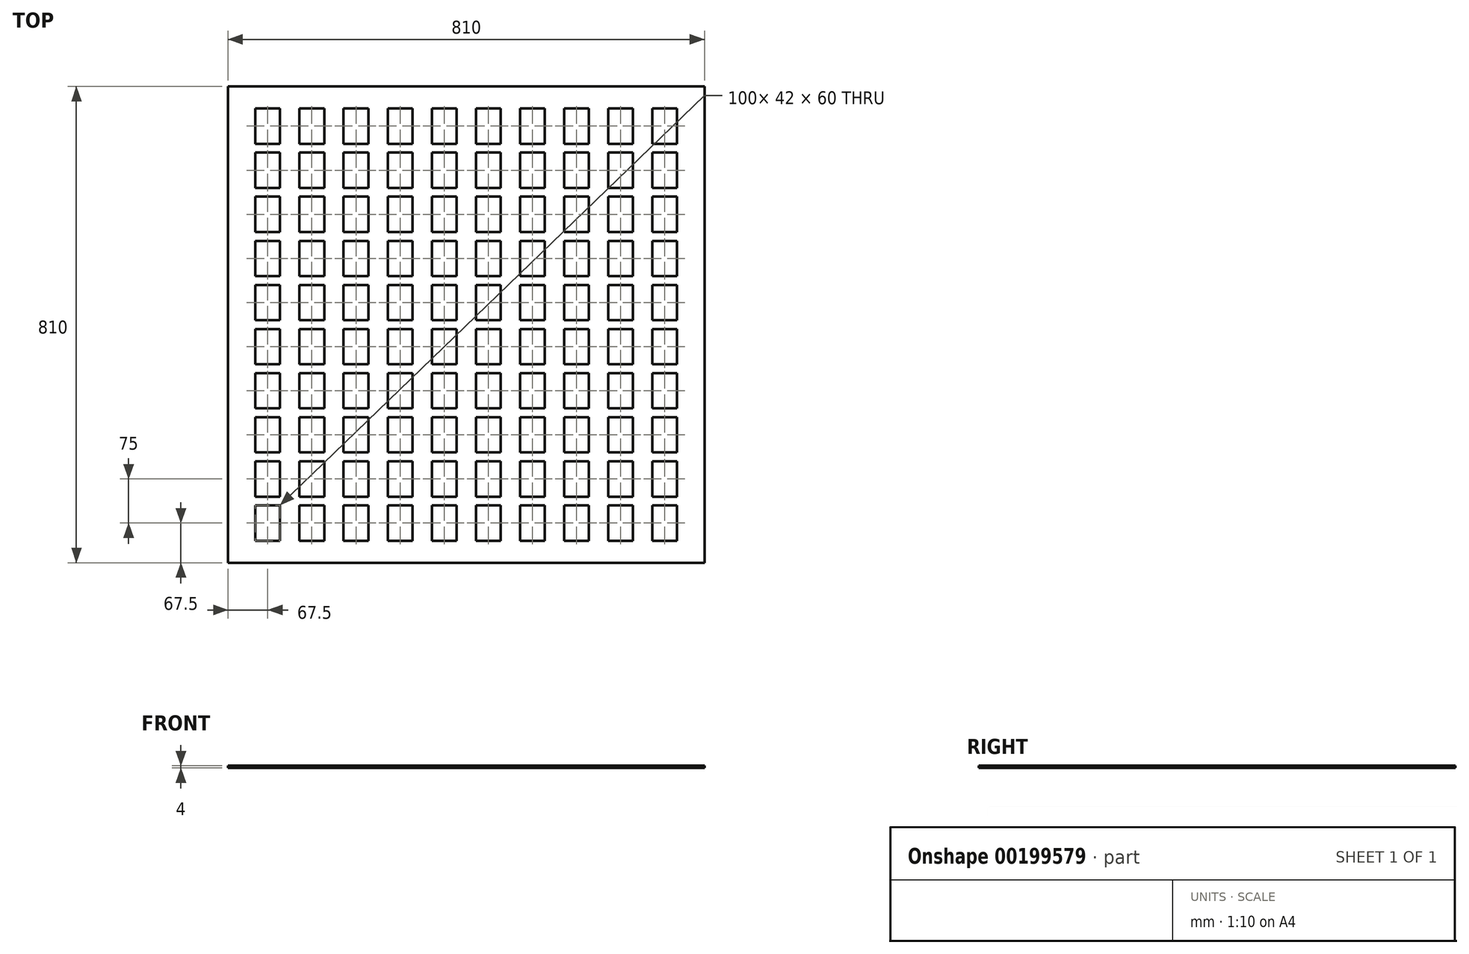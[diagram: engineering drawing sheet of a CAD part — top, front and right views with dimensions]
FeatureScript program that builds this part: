
annotation { "Feature Type Name" : "Feature", "Feature Type Description" : "" }
export const myFeature = defineFeature(function(context is Context, id is Id, definition is map)
    precondition{}
    {
        {
            var Q0;
            Q0=qCreatedBy(makeId("Top.planeOp"),FACE);
            var sketch = newSketch(context, id + "F0", { "sketchPlane" : qUnion([Q0])});
            skLineSegment(sketch, "E0.bottom", {"start": v(-405, 405) * mm, "end": v(405, 405) * mm});
            skLineSegment(sketch, "E0.top", {"start": v(-405, -405) * mm, "end": v(405, -405) * mm});
            skLineSegment(sketch, "E0.left", {"start": v(-405, 405) * mm, "end": v(-405, -405) * mm});
            skLineSegment(sketch, "E0.right", {"start": v(405, 405) * mm, "end": v(405, -405) * mm});
            skSolve(sketch);
        }
        {
            var Q0;
            Q0=makeQuery(id+"F0.imprint","IMPRINT",FACE,{"disambiguationData":[TD([[makeQuery(id+"F0.imprint","IMPRINT",EDGE,{"derivedFrom":sQuery(id+"F0.wireOp",EDGE,"E0.bottom")}),-1.0]])]});
            extrude(context, id + "F1", {"entities" : qUnion([Q0]), "depth" : 4 * mm});
        }
        {
            var Q0;
            Q0=makeQuery(id+"F1.opExtrude","CAP_FACE",FACE,{"disambiguationData":[OSD([sQuery(id+"F0.wireOp",EDGE,"E0.bottom"),sQuery(id+"F0.wireOp",EDGE,"E0.top"),sQuery(id+"F0.wireOp",EDGE,"E0.left"),sQuery(id+"F0.wireOp",EDGE,"E0.right")])],"isStart":false});
            var sketch = newSketch(context, id + "F2", { "sketchPlane" : qUnion([Q0])});
            skCircle(sketch, "E1", {"center": v(-337.5, 337.5) * mm, "radius": 37.5 * mm, "construction": true});
            skLineSegment(sketch, "E2.bottom", {"start": v(-316.5, 307.5) * mm, "end": v(-358.5, 307.5) * mm});
            skLineSegment(sketch, "E2.top", {"start": v(-316.5, 367.5) * mm, "end": v(-358.5, 367.5) * mm});
            skLineSegment(sketch, "E2.left", {"start": v(-316.5, 307.5) * mm, "end": v(-316.5, 367.5) * mm});
            skLineSegment(sketch, "E2.right", {"start": v(-358.5, 307.5) * mm, "end": v(-358.5, 367.5) * mm});
            skLineSegment(sketch, "E3.0.1.0", {"start": v(-316.5, 232.5) * mm, "end": v(-316.5, 292.5) * mm});
            skPoint(sketch, "E3.0.1.1", {"position": v(-337.5, 262.5) * mm});
            skLineSegment(sketch, "E3.0.1.2", {"start": v(-358.5, 232.5) * mm, "end": v(-358.5, 292.5) * mm});
            skCircle(sketch, "E3.0.1.3", {"center": v(-337.5, 262.5) * mm, "radius": 37.5 * mm, "construction": true});
            skLineSegment(sketch, "E3.0.1.4", {"start": v(-316.5, 232.5) * mm, "end": v(-358.5, 232.5) * mm});
            skLineSegment(sketch, "E3.0.1.5", {"start": v(-316.5, 292.5) * mm, "end": v(-358.5, 292.5) * mm});
            skLineSegment(sketch, "E3.0.2.0", {"start": v(-316.5, 157.5) * mm, "end": v(-316.5, 217.5) * mm});
            skPoint(sketch, "E3.0.2.1", {"position": v(-337.5, 187.5) * mm});
            skLineSegment(sketch, "E3.0.2.2", {"start": v(-358.5, 157.5) * mm, "end": v(-358.5, 217.5) * mm});
            skCircle(sketch, "E3.0.2.3", {"center": v(-337.5, 187.5) * mm, "radius": 37.5 * mm, "construction": true});
            skLineSegment(sketch, "E3.0.2.4", {"start": v(-316.5, 157.5) * mm, "end": v(-358.5, 157.5) * mm});
            skLineSegment(sketch, "E3.0.2.5", {"start": v(-316.5, 217.5) * mm, "end": v(-358.5, 217.5) * mm});
            skLineSegment(sketch, "E3.0.3.0", {"start": v(-316.5, 82.5) * mm, "end": v(-316.5, 142.5) * mm});
            skPoint(sketch, "E3.0.3.1", {"position": v(-337.5, 112.5) * mm});
            skLineSegment(sketch, "E3.0.3.2", {"start": v(-358.5, 82.5) * mm, "end": v(-358.5, 142.5) * mm});
            skCircle(sketch, "E3.0.3.3", {"center": v(-337.5, 112.5) * mm, "radius": 37.5 * mm, "construction": true});
            skLineSegment(sketch, "E3.0.3.4", {"start": v(-316.5, 82.5) * mm, "end": v(-358.5, 82.5) * mm});
            skLineSegment(sketch, "E3.0.3.5", {"start": v(-316.5, 142.5) * mm, "end": v(-358.5, 142.5) * mm});
            skLineSegment(sketch, "E3.0.4.0", {"start": v(-316.5, 7.5) * mm, "end": v(-316.5, 67.5) * mm});
            skPoint(sketch, "E3.0.4.1", {"position": v(-337.5, 37.5) * mm});
            skLineSegment(sketch, "E3.0.4.2", {"start": v(-358.5, 7.5) * mm, "end": v(-358.5, 67.5) * mm});
            skCircle(sketch, "E3.0.4.3", {"center": v(-337.5, 37.5) * mm, "radius": 37.5 * mm, "construction": true});
            skLineSegment(sketch, "E3.0.4.4", {"start": v(-316.5, 7.5) * mm, "end": v(-358.5, 7.5) * mm});
            skLineSegment(sketch, "E3.0.4.5", {"start": v(-316.5, 67.5) * mm, "end": v(-358.5, 67.5) * mm});
            skLineSegment(sketch, "E3.0.5.0", {"start": v(-316.5, -67.5) * mm, "end": v(-316.5, -7.5) * mm});
            skPoint(sketch, "E3.0.5.1", {"position": v(-337.5, -37.5) * mm});
            skLineSegment(sketch, "E3.0.5.2", {"start": v(-358.5, -67.5) * mm, "end": v(-358.5, -7.5) * mm});
            skCircle(sketch, "E3.0.5.3", {"center": v(-337.5, -37.5) * mm, "radius": 37.5 * mm, "construction": true});
            skLineSegment(sketch, "E3.0.5.4", {"start": v(-316.5, -67.5) * mm, "end": v(-358.5, -67.5) * mm});
            skLineSegment(sketch, "E3.0.5.5", {"start": v(-316.5, -7.5) * mm, "end": v(-358.5, -7.5) * mm});
            skLineSegment(sketch, "E3.0.6.0", {"start": v(-316.5, -142.5) * mm, "end": v(-316.5, -82.5) * mm});
            skPoint(sketch, "E3.0.6.1", {"position": v(-337.5, -112.5) * mm});
            skLineSegment(sketch, "E3.0.6.2", {"start": v(-358.5, -142.5) * mm, "end": v(-358.5, -82.5) * mm});
            skCircle(sketch, "E3.0.6.3", {"center": v(-337.5, -112.5) * mm, "radius": 37.5 * mm, "construction": true});
            skLineSegment(sketch, "E3.0.6.4", {"start": v(-316.5, -142.5) * mm, "end": v(-358.5, -142.5) * mm});
            skLineSegment(sketch, "E3.0.6.5", {"start": v(-316.5, -82.5) * mm, "end": v(-358.5, -82.5) * mm});
            skLineSegment(sketch, "E3.0.7.0", {"start": v(-316.5, -217.5) * mm, "end": v(-316.5, -157.5) * mm});
            skPoint(sketch, "E3.0.7.1", {"position": v(-337.5, -187.5) * mm});
            skLineSegment(sketch, "E3.0.7.2", {"start": v(-358.5, -217.5) * mm, "end": v(-358.5, -157.5) * mm});
            skCircle(sketch, "E3.0.7.3", {"center": v(-337.5, -187.5) * mm, "radius": 37.5 * mm, "construction": true});
            skLineSegment(sketch, "E3.0.7.4", {"start": v(-316.5, -217.5) * mm, "end": v(-358.5, -217.5) * mm});
            skLineSegment(sketch, "E3.0.7.5", {"start": v(-316.5, -157.5) * mm, "end": v(-358.5, -157.5) * mm});
            skLineSegment(sketch, "E3.0.8.0", {"start": v(-316.5, -292.5) * mm, "end": v(-316.5, -232.5) * mm});
            skPoint(sketch, "E3.0.8.1", {"position": v(-337.5, -262.5) * mm});
            skLineSegment(sketch, "E3.0.8.2", {"start": v(-358.5, -292.5) * mm, "end": v(-358.5, -232.5) * mm});
            skCircle(sketch, "E3.0.8.3", {"center": v(-337.5, -262.5) * mm, "radius": 37.5 * mm, "construction": true});
            skLineSegment(sketch, "E3.0.8.4", {"start": v(-316.5, -292.5) * mm, "end": v(-358.5, -292.5) * mm});
            skLineSegment(sketch, "E3.0.8.5", {"start": v(-316.5, -232.5) * mm, "end": v(-358.5, -232.5) * mm});
            skLineSegment(sketch, "E3.0.9.0", {"start": v(-316.5, -367.5) * mm, "end": v(-316.5, -307.5) * mm});
            skPoint(sketch, "E3.0.9.1", {"position": v(-337.5, -337.5) * mm});
            skLineSegment(sketch, "E3.0.9.2", {"start": v(-358.5, -367.5) * mm, "end": v(-358.5, -307.5) * mm});
            skCircle(sketch, "E3.0.9.3", {"center": v(-337.5, -337.5) * mm, "radius": 37.5 * mm, "construction": true});
            skLineSegment(sketch, "E3.0.9.4", {"start": v(-316.5, -367.5) * mm, "end": v(-358.5, -367.5) * mm});
            skLineSegment(sketch, "E3.0.9.5", {"start": v(-316.5, -307.5) * mm, "end": v(-358.5, -307.5) * mm});
            skLineSegment(sketch, "E3.1.0.0", {"start": v(-241.5, 307.5) * mm, "end": v(-241.5, 367.5) * mm});
            skPoint(sketch, "E3.1.0.1", {"position": v(-262.5, 337.5) * mm});
            skLineSegment(sketch, "E3.1.0.2", {"start": v(-283.5, 307.5) * mm, "end": v(-283.5, 367.5) * mm});
            skCircle(sketch, "E3.1.0.3", {"center": v(-262.5, 337.5) * mm, "radius": 37.5 * mm, "construction": true});
            skLineSegment(sketch, "E3.1.0.4", {"start": v(-241.5, 307.5) * mm, "end": v(-283.5, 307.5) * mm});
            skLineSegment(sketch, "E3.1.0.5", {"start": v(-241.5, 367.5) * mm, "end": v(-283.5, 367.5) * mm});
            skLineSegment(sketch, "E3.1.1.0", {"start": v(-241.5, 232.5) * mm, "end": v(-241.5, 292.5) * mm});
            skPoint(sketch, "E3.1.1.1", {"position": v(-262.5, 262.5) * mm});
            skLineSegment(sketch, "E3.1.1.2", {"start": v(-283.5, 232.5) * mm, "end": v(-283.5, 292.5) * mm});
            skCircle(sketch, "E3.1.1.3", {"center": v(-262.5, 262.5) * mm, "radius": 37.5 * mm, "construction": true});
            skLineSegment(sketch, "E3.1.1.4", {"start": v(-241.5, 232.5) * mm, "end": v(-283.5, 232.5) * mm});
            skLineSegment(sketch, "E3.1.1.5", {"start": v(-241.5, 292.5) * mm, "end": v(-283.5, 292.5) * mm});
            skLineSegment(sketch, "E3.1.2.0", {"start": v(-241.5, 157.5) * mm, "end": v(-241.5, 217.5) * mm});
            skPoint(sketch, "E3.1.2.1", {"position": v(-262.5, 187.5) * mm});
            skLineSegment(sketch, "E3.1.2.2", {"start": v(-283.5, 157.5) * mm, "end": v(-283.5, 217.5) * mm});
            skCircle(sketch, "E3.1.2.3", {"center": v(-262.5, 187.5) * mm, "radius": 37.5 * mm, "construction": true});
            skLineSegment(sketch, "E3.1.2.4", {"start": v(-241.5, 157.5) * mm, "end": v(-283.5, 157.5) * mm});
            skLineSegment(sketch, "E3.1.2.5", {"start": v(-241.5, 217.5) * mm, "end": v(-283.5, 217.5) * mm});
            skLineSegment(sketch, "E3.1.3.0", {"start": v(-241.5, 82.5) * mm, "end": v(-241.5, 142.5) * mm});
            skPoint(sketch, "E3.1.3.1", {"position": v(-262.5, 112.5) * mm});
            skLineSegment(sketch, "E3.1.3.2", {"start": v(-283.5, 82.5) * mm, "end": v(-283.5, 142.5) * mm});
            skCircle(sketch, "E3.1.3.3", {"center": v(-262.5, 112.5) * mm, "radius": 37.5 * mm, "construction": true});
            skLineSegment(sketch, "E3.1.3.4", {"start": v(-241.5, 82.5) * mm, "end": v(-283.5, 82.5) * mm});
            skLineSegment(sketch, "E3.1.3.5", {"start": v(-241.5, 142.5) * mm, "end": v(-283.5, 142.5) * mm});
            skLineSegment(sketch, "E3.1.4.0", {"start": v(-241.5, 7.5) * mm, "end": v(-241.5, 67.5) * mm});
            skPoint(sketch, "E3.1.4.1", {"position": v(-262.5, 37.5) * mm});
            skLineSegment(sketch, "E3.1.4.2", {"start": v(-283.5, 7.5) * mm, "end": v(-283.5, 67.5) * mm});
            skCircle(sketch, "E3.1.4.3", {"center": v(-262.5, 37.5) * mm, "radius": 37.5 * mm, "construction": true});
            skLineSegment(sketch, "E3.1.4.4", {"start": v(-241.5, 7.5) * mm, "end": v(-283.5, 7.5) * mm});
            skLineSegment(sketch, "E3.1.4.5", {"start": v(-241.5, 67.5) * mm, "end": v(-283.5, 67.5) * mm});
            skLineSegment(sketch, "E3.1.5.0", {"start": v(-241.5, -67.5) * mm, "end": v(-241.5, -7.5) * mm});
            skPoint(sketch, "E3.1.5.1", {"position": v(-262.5, -37.5) * mm});
            skLineSegment(sketch, "E3.1.5.2", {"start": v(-283.5, -67.5) * mm, "end": v(-283.5, -7.5) * mm});
            skCircle(sketch, "E3.1.5.3", {"center": v(-262.5, -37.5) * mm, "radius": 37.5 * mm, "construction": true});
            skLineSegment(sketch, "E3.1.5.4", {"start": v(-241.5, -67.5) * mm, "end": v(-283.5, -67.5) * mm});
            skLineSegment(sketch, "E3.1.5.5", {"start": v(-241.5, -7.5) * mm, "end": v(-283.5, -7.5) * mm});
            skLineSegment(sketch, "E3.1.6.0", {"start": v(-241.5, -142.5) * mm, "end": v(-241.5, -82.5) * mm});
            skPoint(sketch, "E3.1.6.1", {"position": v(-262.5, -112.5) * mm});
            skLineSegment(sketch, "E3.1.6.2", {"start": v(-283.5, -142.5) * mm, "end": v(-283.5, -82.5) * mm});
            skCircle(sketch, "E3.1.6.3", {"center": v(-262.5, -112.5) * mm, "radius": 37.5 * mm, "construction": true});
            skLineSegment(sketch, "E3.1.6.4", {"start": v(-241.5, -142.5) * mm, "end": v(-283.5, -142.5) * mm});
            skLineSegment(sketch, "E3.1.6.5", {"start": v(-241.5, -82.5) * mm, "end": v(-283.5, -82.5) * mm});
            skLineSegment(sketch, "E3.1.7.0", {"start": v(-241.5, -217.5) * mm, "end": v(-241.5, -157.5) * mm});
            skPoint(sketch, "E3.1.7.1", {"position": v(-262.5, -187.5) * mm});
            skLineSegment(sketch, "E3.1.7.2", {"start": v(-283.5, -217.5) * mm, "end": v(-283.5, -157.5) * mm});
            skCircle(sketch, "E3.1.7.3", {"center": v(-262.5, -187.5) * mm, "radius": 37.5 * mm, "construction": true});
            skLineSegment(sketch, "E3.1.7.4", {"start": v(-241.5, -217.5) * mm, "end": v(-283.5, -217.5) * mm});
            skLineSegment(sketch, "E3.1.7.5", {"start": v(-241.5, -157.5) * mm, "end": v(-283.5, -157.5) * mm});
            skLineSegment(sketch, "E3.1.8.0", {"start": v(-241.5, -292.5) * mm, "end": v(-241.5, -232.5) * mm});
            skPoint(sketch, "E3.1.8.1", {"position": v(-262.5, -262.5) * mm});
            skLineSegment(sketch, "E3.1.8.2", {"start": v(-283.5, -292.5) * mm, "end": v(-283.5, -232.5) * mm});
            skCircle(sketch, "E3.1.8.3", {"center": v(-262.5, -262.5) * mm, "radius": 37.5 * mm, "construction": true});
            skLineSegment(sketch, "E3.1.8.4", {"start": v(-241.5, -292.5) * mm, "end": v(-283.5, -292.5) * mm});
            skLineSegment(sketch, "E3.1.8.5", {"start": v(-241.5, -232.5) * mm, "end": v(-283.5, -232.5) * mm});
            skLineSegment(sketch, "E3.1.9.0", {"start": v(-241.5, -367.5) * mm, "end": v(-241.5, -307.5) * mm});
            skPoint(sketch, "E3.1.9.1", {"position": v(-262.5, -337.5) * mm});
            skLineSegment(sketch, "E3.1.9.2", {"start": v(-283.5, -367.5) * mm, "end": v(-283.5, -307.5) * mm});
            skCircle(sketch, "E3.1.9.3", {"center": v(-262.5, -337.5) * mm, "radius": 37.5 * mm, "construction": true});
            skLineSegment(sketch, "E3.1.9.4", {"start": v(-241.5, -367.5) * mm, "end": v(-283.5, -367.5) * mm});
            skLineSegment(sketch, "E3.1.9.5", {"start": v(-241.5, -307.5) * mm, "end": v(-283.5, -307.5) * mm});
            skLineSegment(sketch, "E3.2.0.0", {"start": v(-166.5, 307.5) * mm, "end": v(-166.5, 367.5) * mm});
            skPoint(sketch, "E3.2.0.1", {"position": v(-187.5, 337.5) * mm});
            skLineSegment(sketch, "E3.2.0.2", {"start": v(-208.5, 307.5) * mm, "end": v(-208.5, 367.5) * mm});
            skCircle(sketch, "E3.2.0.3", {"center": v(-187.5, 337.5) * mm, "radius": 37.5 * mm, "construction": true});
            skLineSegment(sketch, "E3.2.0.4", {"start": v(-166.5, 307.5) * mm, "end": v(-208.5, 307.5) * mm});
            skLineSegment(sketch, "E3.2.0.5", {"start": v(-166.5, 367.5) * mm, "end": v(-208.5, 367.5) * mm});
            skLineSegment(sketch, "E3.2.1.0", {"start": v(-166.5, 232.5) * mm, "end": v(-166.5, 292.5) * mm});
            skPoint(sketch, "E3.2.1.1", {"position": v(-187.5, 262.5) * mm});
            skLineSegment(sketch, "E3.2.1.2", {"start": v(-208.5, 232.5) * mm, "end": v(-208.5, 292.5) * mm});
            skCircle(sketch, "E3.2.1.3", {"center": v(-187.5, 262.5) * mm, "radius": 37.5 * mm, "construction": true});
            skLineSegment(sketch, "E3.2.1.4", {"start": v(-166.5, 232.5) * mm, "end": v(-208.5, 232.5) * mm});
            skLineSegment(sketch, "E3.2.1.5", {"start": v(-166.5, 292.5) * mm, "end": v(-208.5, 292.5) * mm});
            skLineSegment(sketch, "E3.2.2.0", {"start": v(-166.5, 157.5) * mm, "end": v(-166.5, 217.5) * mm});
            skPoint(sketch, "E3.2.2.1", {"position": v(-187.5, 187.5) * mm});
            skLineSegment(sketch, "E3.2.2.2", {"start": v(-208.5, 157.5) * mm, "end": v(-208.5, 217.5) * mm});
            skCircle(sketch, "E3.2.2.3", {"center": v(-187.5, 187.5) * mm, "radius": 37.5 * mm, "construction": true});
            skLineSegment(sketch, "E3.2.2.4", {"start": v(-166.5, 157.5) * mm, "end": v(-208.5, 157.5) * mm});
            skLineSegment(sketch, "E3.2.2.5", {"start": v(-166.5, 217.5) * mm, "end": v(-208.5, 217.5) * mm});
            skLineSegment(sketch, "E3.2.3.0", {"start": v(-166.5, 82.5) * mm, "end": v(-166.5, 142.5) * mm});
            skPoint(sketch, "E3.2.3.1", {"position": v(-187.5, 112.5) * mm});
            skLineSegment(sketch, "E3.2.3.2", {"start": v(-208.5, 82.5) * mm, "end": v(-208.5, 142.5) * mm});
            skCircle(sketch, "E3.2.3.3", {"center": v(-187.5, 112.5) * mm, "radius": 37.5 * mm, "construction": true});
            skLineSegment(sketch, "E3.2.3.4", {"start": v(-166.5, 82.5) * mm, "end": v(-208.5, 82.5) * mm});
            skLineSegment(sketch, "E3.2.3.5", {"start": v(-166.5, 142.5) * mm, "end": v(-208.5, 142.5) * mm});
            skLineSegment(sketch, "E3.2.4.0", {"start": v(-166.5, 7.5) * mm, "end": v(-166.5, 67.5) * mm});
            skPoint(sketch, "E3.2.4.1", {"position": v(-187.5, 37.5) * mm});
            skLineSegment(sketch, "E3.2.4.2", {"start": v(-208.5, 7.5) * mm, "end": v(-208.5, 67.5) * mm});
            skCircle(sketch, "E3.2.4.3", {"center": v(-187.5, 37.5) * mm, "radius": 37.5 * mm, "construction": true});
            skLineSegment(sketch, "E3.2.4.4", {"start": v(-166.5, 7.5) * mm, "end": v(-208.5, 7.5) * mm});
            skLineSegment(sketch, "E3.2.4.5", {"start": v(-166.5, 67.5) * mm, "end": v(-208.5, 67.5) * mm});
            skLineSegment(sketch, "E3.2.5.0", {"start": v(-166.5, -67.5) * mm, "end": v(-166.5, -7.5) * mm});
            skPoint(sketch, "E3.2.5.1", {"position": v(-187.5, -37.5) * mm});
            skLineSegment(sketch, "E3.2.5.2", {"start": v(-208.5, -67.5) * mm, "end": v(-208.5, -7.5) * mm});
            skCircle(sketch, "E3.2.5.3", {"center": v(-187.5, -37.5) * mm, "radius": 37.5 * mm, "construction": true});
            skLineSegment(sketch, "E3.2.5.4", {"start": v(-166.5, -67.5) * mm, "end": v(-208.5, -67.5) * mm});
            skLineSegment(sketch, "E3.2.5.5", {"start": v(-166.5, -7.5) * mm, "end": v(-208.5, -7.5) * mm});
            skLineSegment(sketch, "E3.2.6.0", {"start": v(-166.5, -142.5) * mm, "end": v(-166.5, -82.5) * mm});
            skPoint(sketch, "E3.2.6.1", {"position": v(-187.5, -112.5) * mm});
            skLineSegment(sketch, "E3.2.6.2", {"start": v(-208.5, -142.5) * mm, "end": v(-208.5, -82.5) * mm});
            skCircle(sketch, "E3.2.6.3", {"center": v(-187.5, -112.5) * mm, "radius": 37.5 * mm, "construction": true});
            skLineSegment(sketch, "E3.2.6.4", {"start": v(-166.5, -142.5) * mm, "end": v(-208.5, -142.5) * mm});
            skLineSegment(sketch, "E3.2.6.5", {"start": v(-166.5, -82.5) * mm, "end": v(-208.5, -82.5) * mm});
            skLineSegment(sketch, "E3.2.7.0", {"start": v(-166.5, -217.5) * mm, "end": v(-166.5, -157.5) * mm});
            skPoint(sketch, "E3.2.7.1", {"position": v(-187.5, -187.5) * mm});
            skLineSegment(sketch, "E3.2.7.2", {"start": v(-208.5, -217.5) * mm, "end": v(-208.5, -157.5) * mm});
            skCircle(sketch, "E3.2.7.3", {"center": v(-187.5, -187.5) * mm, "radius": 37.5 * mm, "construction": true});
            skLineSegment(sketch, "E3.2.7.4", {"start": v(-166.5, -217.5) * mm, "end": v(-208.5, -217.5) * mm});
            skLineSegment(sketch, "E3.2.7.5", {"start": v(-166.5, -157.5) * mm, "end": v(-208.5, -157.5) * mm});
            skLineSegment(sketch, "E3.2.8.0", {"start": v(-166.5, -292.5) * mm, "end": v(-166.5, -232.5) * mm});
            skPoint(sketch, "E3.2.8.1", {"position": v(-187.5, -262.5) * mm});
            skLineSegment(sketch, "E3.2.8.2", {"start": v(-208.5, -292.5) * mm, "end": v(-208.5, -232.5) * mm});
            skCircle(sketch, "E3.2.8.3", {"center": v(-187.5, -262.5) * mm, "radius": 37.5 * mm, "construction": true});
            skLineSegment(sketch, "E3.2.8.4", {"start": v(-166.5, -292.5) * mm, "end": v(-208.5, -292.5) * mm});
            skLineSegment(sketch, "E3.2.8.5", {"start": v(-166.5, -232.5) * mm, "end": v(-208.5, -232.5) * mm});
            skLineSegment(sketch, "E3.2.9.0", {"start": v(-166.5, -367.5) * mm, "end": v(-166.5, -307.5) * mm});
            skPoint(sketch, "E3.2.9.1", {"position": v(-187.5, -337.5) * mm});
            skLineSegment(sketch, "E3.2.9.2", {"start": v(-208.5, -367.5) * mm, "end": v(-208.5, -307.5) * mm});
            skCircle(sketch, "E3.2.9.3", {"center": v(-187.5, -337.5) * mm, "radius": 37.5 * mm, "construction": true});
            skLineSegment(sketch, "E3.2.9.4", {"start": v(-166.5, -367.5) * mm, "end": v(-208.5, -367.5) * mm});
            skLineSegment(sketch, "E3.2.9.5", {"start": v(-166.5, -307.5) * mm, "end": v(-208.5, -307.5) * mm});
            skLineSegment(sketch, "E3.3.0.0", {"start": v(-91.5, 307.5) * mm, "end": v(-91.5, 367.5) * mm});
            skPoint(sketch, "E3.3.0.1", {"position": v(-112.5, 337.5) * mm});
            skLineSegment(sketch, "E3.3.0.2", {"start": v(-133.5, 307.5) * mm, "end": v(-133.5, 367.5) * mm});
            skCircle(sketch, "E3.3.0.3", {"center": v(-112.5, 337.5) * mm, "radius": 37.5 * mm, "construction": true});
            skLineSegment(sketch, "E3.3.0.4", {"start": v(-91.5, 307.5) * mm, "end": v(-133.5, 307.5) * mm});
            skLineSegment(sketch, "E3.3.0.5", {"start": v(-91.5, 367.5) * mm, "end": v(-133.5, 367.5) * mm});
            skLineSegment(sketch, "E3.3.1.0", {"start": v(-91.5, 232.5) * mm, "end": v(-91.5, 292.5) * mm});
            skPoint(sketch, "E3.3.1.1", {"position": v(-112.5, 262.5) * mm});
            skLineSegment(sketch, "E3.3.1.2", {"start": v(-133.5, 232.5) * mm, "end": v(-133.5, 292.5) * mm});
            skCircle(sketch, "E3.3.1.3", {"center": v(-112.5, 262.5) * mm, "radius": 37.5 * mm, "construction": true});
            skLineSegment(sketch, "E3.3.1.4", {"start": v(-91.5, 232.5) * mm, "end": v(-133.5, 232.5) * mm});
            skLineSegment(sketch, "E3.3.1.5", {"start": v(-91.5, 292.5) * mm, "end": v(-133.5, 292.5) * mm});
            skLineSegment(sketch, "E3.3.2.0", {"start": v(-91.5, 157.5) * mm, "end": v(-91.5, 217.5) * mm});
            skPoint(sketch, "E3.3.2.1", {"position": v(-112.5, 187.5) * mm});
            skLineSegment(sketch, "E3.3.2.2", {"start": v(-133.5, 157.5) * mm, "end": v(-133.5, 217.5) * mm});
            skCircle(sketch, "E3.3.2.3", {"center": v(-112.5, 187.5) * mm, "radius": 37.5 * mm, "construction": true});
            skLineSegment(sketch, "E3.3.2.4", {"start": v(-91.5, 157.5) * mm, "end": v(-133.5, 157.5) * mm});
            skLineSegment(sketch, "E3.3.2.5", {"start": v(-91.5, 217.5) * mm, "end": v(-133.5, 217.5) * mm});
            skLineSegment(sketch, "E3.3.3.0", {"start": v(-91.5, 82.5) * mm, "end": v(-91.5, 142.5) * mm});
            skPoint(sketch, "E3.3.3.1", {"position": v(-112.5, 112.5) * mm});
            skLineSegment(sketch, "E3.3.3.2", {"start": v(-133.5, 82.5) * mm, "end": v(-133.5, 142.5) * mm});
            skCircle(sketch, "E3.3.3.3", {"center": v(-112.5, 112.5) * mm, "radius": 37.5 * mm, "construction": true});
            skLineSegment(sketch, "E3.3.3.4", {"start": v(-91.5, 82.5) * mm, "end": v(-133.5, 82.5) * mm});
            skLineSegment(sketch, "E3.3.3.5", {"start": v(-91.5, 142.5) * mm, "end": v(-133.5, 142.5) * mm});
            skLineSegment(sketch, "E3.3.4.0", {"start": v(-91.5, 7.5) * mm, "end": v(-91.5, 67.5) * mm});
            skPoint(sketch, "E3.3.4.1", {"position": v(-112.5, 37.5) * mm});
            skLineSegment(sketch, "E3.3.4.2", {"start": v(-133.5, 7.5) * mm, "end": v(-133.5, 67.5) * mm});
            skCircle(sketch, "E3.3.4.3", {"center": v(-112.5, 37.5) * mm, "radius": 37.5 * mm, "construction": true});
            skLineSegment(sketch, "E3.3.4.4", {"start": v(-91.5, 7.5) * mm, "end": v(-133.5, 7.5) * mm});
            skLineSegment(sketch, "E3.3.4.5", {"start": v(-91.5, 67.5) * mm, "end": v(-133.5, 67.5) * mm});
            skLineSegment(sketch, "E3.3.5.0", {"start": v(-91.5, -67.5) * mm, "end": v(-91.5, -7.5) * mm});
            skPoint(sketch, "E3.3.5.1", {"position": v(-112.5, -37.5) * mm});
            skLineSegment(sketch, "E3.3.5.2", {"start": v(-133.5, -67.5) * mm, "end": v(-133.5, -7.5) * mm});
            skCircle(sketch, "E3.3.5.3", {"center": v(-112.5, -37.5) * mm, "radius": 37.5 * mm, "construction": true});
            skLineSegment(sketch, "E3.3.5.4", {"start": v(-91.5, -67.5) * mm, "end": v(-133.5, -67.5) * mm});
            skLineSegment(sketch, "E3.3.5.5", {"start": v(-91.5, -7.5) * mm, "end": v(-133.5, -7.5) * mm});
            skLineSegment(sketch, "E3.3.6.0", {"start": v(-91.5, -142.5) * mm, "end": v(-91.5, -82.5) * mm});
            skPoint(sketch, "E3.3.6.1", {"position": v(-112.5, -112.5) * mm});
            skLineSegment(sketch, "E3.3.6.2", {"start": v(-133.5, -142.5) * mm, "end": v(-133.5, -82.5) * mm});
            skCircle(sketch, "E3.3.6.3", {"center": v(-112.5, -112.5) * mm, "radius": 37.5 * mm, "construction": true});
            skLineSegment(sketch, "E3.3.6.4", {"start": v(-91.5, -142.5) * mm, "end": v(-133.5, -142.5) * mm});
            skLineSegment(sketch, "E3.3.6.5", {"start": v(-91.5, -82.5) * mm, "end": v(-133.5, -82.5) * mm});
            skLineSegment(sketch, "E3.3.7.0", {"start": v(-91.5, -217.5) * mm, "end": v(-91.5, -157.5) * mm});
            skPoint(sketch, "E3.3.7.1", {"position": v(-112.5, -187.5) * mm});
            skLineSegment(sketch, "E3.3.7.2", {"start": v(-133.5, -217.5) * mm, "end": v(-133.5, -157.5) * mm});
            skCircle(sketch, "E3.3.7.3", {"center": v(-112.5, -187.5) * mm, "radius": 37.5 * mm, "construction": true});
            skLineSegment(sketch, "E3.3.7.4", {"start": v(-91.5, -217.5) * mm, "end": v(-133.5, -217.5) * mm});
            skLineSegment(sketch, "E3.3.7.5", {"start": v(-91.5, -157.5) * mm, "end": v(-133.5, -157.5) * mm});
            skLineSegment(sketch, "E3.3.8.0", {"start": v(-91.5, -292.5) * mm, "end": v(-91.5, -232.5) * mm});
            skPoint(sketch, "E3.3.8.1", {"position": v(-112.5, -262.5) * mm});
            skLineSegment(sketch, "E3.3.8.2", {"start": v(-133.5, -292.5) * mm, "end": v(-133.5, -232.5) * mm});
            skCircle(sketch, "E3.3.8.3", {"center": v(-112.5, -262.5) * mm, "radius": 37.5 * mm, "construction": true});
            skLineSegment(sketch, "E3.3.8.4", {"start": v(-91.5, -292.5) * mm, "end": v(-133.5, -292.5) * mm});
            skLineSegment(sketch, "E3.3.8.5", {"start": v(-91.5, -232.5) * mm, "end": v(-133.5, -232.5) * mm});
            skLineSegment(sketch, "E3.3.9.0", {"start": v(-91.5, -367.5) * mm, "end": v(-91.5, -307.5) * mm});
            skPoint(sketch, "E3.3.9.1", {"position": v(-112.5, -337.5) * mm});
            skLineSegment(sketch, "E3.3.9.2", {"start": v(-133.5, -367.5) * mm, "end": v(-133.5, -307.5) * mm});
            skCircle(sketch, "E3.3.9.3", {"center": v(-112.5, -337.5) * mm, "radius": 37.5 * mm, "construction": true});
            skLineSegment(sketch, "E3.3.9.4", {"start": v(-91.5, -367.5) * mm, "end": v(-133.5, -367.5) * mm});
            skLineSegment(sketch, "E3.3.9.5", {"start": v(-91.5, -307.5) * mm, "end": v(-133.5, -307.5) * mm});
            skLineSegment(sketch, "E3.4.0.0", {"start": v(-16.5, 307.5) * mm, "end": v(-16.5, 367.5) * mm});
            skPoint(sketch, "E3.4.0.1", {"position": v(-37.5, 337.5) * mm});
            skLineSegment(sketch, "E3.4.0.2", {"start": v(-58.5, 307.5) * mm, "end": v(-58.5, 367.5) * mm});
            skCircle(sketch, "E3.4.0.3", {"center": v(-37.5, 337.5) * mm, "radius": 37.5 * mm, "construction": true});
            skLineSegment(sketch, "E3.4.0.4", {"start": v(-16.5, 307.5) * mm, "end": v(-58.5, 307.5) * mm});
            skLineSegment(sketch, "E3.4.0.5", {"start": v(-16.5, 367.5) * mm, "end": v(-58.5, 367.5) * mm});
            skLineSegment(sketch, "E3.4.1.0", {"start": v(-16.5, 232.5) * mm, "end": v(-16.5, 292.5) * mm});
            skPoint(sketch, "E3.4.1.1", {"position": v(-37.5, 262.5) * mm});
            skLineSegment(sketch, "E3.4.1.2", {"start": v(-58.5, 232.5) * mm, "end": v(-58.5, 292.5) * mm});
            skCircle(sketch, "E3.4.1.3", {"center": v(-37.5, 262.5) * mm, "radius": 37.5 * mm, "construction": true});
            skLineSegment(sketch, "E3.4.1.4", {"start": v(-16.5, 232.5) * mm, "end": v(-58.5, 232.5) * mm});
            skLineSegment(sketch, "E3.4.1.5", {"start": v(-16.5, 292.5) * mm, "end": v(-58.5, 292.5) * mm});
            skLineSegment(sketch, "E3.4.2.0", {"start": v(-16.5, 157.5) * mm, "end": v(-16.5, 217.5) * mm});
            skPoint(sketch, "E3.4.2.1", {"position": v(-37.5, 187.5) * mm});
            skLineSegment(sketch, "E3.4.2.2", {"start": v(-58.5, 157.5) * mm, "end": v(-58.5, 217.5) * mm});
            skCircle(sketch, "E3.4.2.3", {"center": v(-37.5, 187.5) * mm, "radius": 37.5 * mm, "construction": true});
            skLineSegment(sketch, "E3.4.2.4", {"start": v(-16.5, 157.5) * mm, "end": v(-58.5, 157.5) * mm});
            skLineSegment(sketch, "E3.4.2.5", {"start": v(-16.5, 217.5) * mm, "end": v(-58.5, 217.5) * mm});
            skLineSegment(sketch, "E3.4.3.0", {"start": v(-16.5, 82.5) * mm, "end": v(-16.5, 142.5) * mm});
            skPoint(sketch, "E3.4.3.1", {"position": v(-37.5, 112.5) * mm});
            skLineSegment(sketch, "E3.4.3.2", {"start": v(-58.5, 82.5) * mm, "end": v(-58.5, 142.5) * mm});
            skCircle(sketch, "E3.4.3.3", {"center": v(-37.5, 112.5) * mm, "radius": 37.5 * mm, "construction": true});
            skLineSegment(sketch, "E3.4.3.4", {"start": v(-16.5, 82.5) * mm, "end": v(-58.5, 82.5) * mm});
            skLineSegment(sketch, "E3.4.3.5", {"start": v(-16.5, 142.5) * mm, "end": v(-58.5, 142.5) * mm});
            skLineSegment(sketch, "E3.4.4.0", {"start": v(-16.5, 7.5) * mm, "end": v(-16.5, 67.5) * mm});
            skPoint(sketch, "E3.4.4.1", {"position": v(-37.5, 37.5) * mm});
            skLineSegment(sketch, "E3.4.4.2", {"start": v(-58.5, 7.5) * mm, "end": v(-58.5, 67.5) * mm});
            skCircle(sketch, "E3.4.4.3", {"center": v(-37.5, 37.5) * mm, "radius": 37.5 * mm, "construction": true});
            skLineSegment(sketch, "E3.4.4.4", {"start": v(-16.5, 7.5) * mm, "end": v(-58.5, 7.5) * mm});
            skLineSegment(sketch, "E3.4.4.5", {"start": v(-16.5, 67.5) * mm, "end": v(-58.5, 67.5) * mm});
            skLineSegment(sketch, "E3.4.5.0", {"start": v(-16.5, -67.5) * mm, "end": v(-16.5, -7.5) * mm});
            skPoint(sketch, "E3.4.5.1", {"position": v(-37.5, -37.5) * mm});
            skLineSegment(sketch, "E3.4.5.2", {"start": v(-58.5, -67.5) * mm, "end": v(-58.5, -7.5) * mm});
            skCircle(sketch, "E3.4.5.3", {"center": v(-37.5, -37.5) * mm, "radius": 37.5 * mm, "construction": true});
            skLineSegment(sketch, "E3.4.5.4", {"start": v(-16.5, -67.5) * mm, "end": v(-58.5, -67.5) * mm});
            skLineSegment(sketch, "E3.4.5.5", {"start": v(-16.5, -7.5) * mm, "end": v(-58.5, -7.5) * mm});
            skLineSegment(sketch, "E3.4.6.0", {"start": v(-16.5, -142.5) * mm, "end": v(-16.5, -82.5) * mm});
            skPoint(sketch, "E3.4.6.1", {"position": v(-37.5, -112.5) * mm});
            skLineSegment(sketch, "E3.4.6.2", {"start": v(-58.5, -142.5) * mm, "end": v(-58.5, -82.5) * mm});
            skCircle(sketch, "E3.4.6.3", {"center": v(-37.5, -112.5) * mm, "radius": 37.5 * mm, "construction": true});
            skLineSegment(sketch, "E3.4.6.4", {"start": v(-16.5, -142.5) * mm, "end": v(-58.5, -142.5) * mm});
            skLineSegment(sketch, "E3.4.6.5", {"start": v(-16.5, -82.5) * mm, "end": v(-58.5, -82.5) * mm});
            skLineSegment(sketch, "E3.4.7.0", {"start": v(-16.5, -217.5) * mm, "end": v(-16.5, -157.5) * mm});
            skPoint(sketch, "E3.4.7.1", {"position": v(-37.5, -187.5) * mm});
            skLineSegment(sketch, "E3.4.7.2", {"start": v(-58.5, -217.5) * mm, "end": v(-58.5, -157.5) * mm});
            skCircle(sketch, "E3.4.7.3", {"center": v(-37.5, -187.5) * mm, "radius": 37.5 * mm, "construction": true});
            skLineSegment(sketch, "E3.4.7.4", {"start": v(-16.5, -217.5) * mm, "end": v(-58.5, -217.5) * mm});
            skLineSegment(sketch, "E3.4.7.5", {"start": v(-16.5, -157.5) * mm, "end": v(-58.5, -157.5) * mm});
            skLineSegment(sketch, "E3.4.8.0", {"start": v(-16.5, -292.5) * mm, "end": v(-16.5, -232.5) * mm});
            skPoint(sketch, "E3.4.8.1", {"position": v(-37.5, -262.5) * mm});
            skLineSegment(sketch, "E3.4.8.2", {"start": v(-58.5, -292.5) * mm, "end": v(-58.5, -232.5) * mm});
            skCircle(sketch, "E3.4.8.3", {"center": v(-37.5, -262.5) * mm, "radius": 37.5 * mm, "construction": true});
            skLineSegment(sketch, "E3.4.8.4", {"start": v(-16.5, -292.5) * mm, "end": v(-58.5, -292.5) * mm});
            skLineSegment(sketch, "E3.4.8.5", {"start": v(-16.5, -232.5) * mm, "end": v(-58.5, -232.5) * mm});
            skLineSegment(sketch, "E3.4.9.0", {"start": v(-16.5, -367.5) * mm, "end": v(-16.5, -307.5) * mm});
            skPoint(sketch, "E3.4.9.1", {"position": v(-37.5, -337.5) * mm});
            skLineSegment(sketch, "E3.4.9.2", {"start": v(-58.5, -367.5) * mm, "end": v(-58.5, -307.5) * mm});
            skCircle(sketch, "E3.4.9.3", {"center": v(-37.5, -337.5) * mm, "radius": 37.5 * mm, "construction": true});
            skLineSegment(sketch, "E3.4.9.4", {"start": v(-16.5, -367.5) * mm, "end": v(-58.5, -367.5) * mm});
            skLineSegment(sketch, "E3.4.9.5", {"start": v(-16.5, -307.5) * mm, "end": v(-58.5, -307.5) * mm});
            skLineSegment(sketch, "E3.5.0.0", {"start": v(58.5, 307.5) * mm, "end": v(58.5, 367.5) * mm});
            skPoint(sketch, "E3.5.0.1", {"position": v(37.5, 337.5) * mm});
            skLineSegment(sketch, "E3.5.0.2", {"start": v(16.5, 307.5) * mm, "end": v(16.5, 367.5) * mm});
            skCircle(sketch, "E3.5.0.3", {"center": v(37.5, 337.5) * mm, "radius": 37.5 * mm, "construction": true});
            skLineSegment(sketch, "E3.5.0.4", {"start": v(58.5, 307.5) * mm, "end": v(16.5, 307.5) * mm});
            skLineSegment(sketch, "E3.5.0.5", {"start": v(58.5, 367.5) * mm, "end": v(16.5, 367.5) * mm});
            skLineSegment(sketch, "E3.5.1.0", {"start": v(58.5, 232.5) * mm, "end": v(58.5, 292.5) * mm});
            skPoint(sketch, "E3.5.1.1", {"position": v(37.5, 262.5) * mm});
            skLineSegment(sketch, "E3.5.1.2", {"start": v(16.5, 232.5) * mm, "end": v(16.5, 292.5) * mm});
            skCircle(sketch, "E3.5.1.3", {"center": v(37.5, 262.5) * mm, "radius": 37.5 * mm, "construction": true});
            skLineSegment(sketch, "E3.5.1.4", {"start": v(58.5, 232.5) * mm, "end": v(16.5, 232.5) * mm});
            skLineSegment(sketch, "E3.5.1.5", {"start": v(58.5, 292.5) * mm, "end": v(16.5, 292.5) * mm});
            skLineSegment(sketch, "E3.5.2.0", {"start": v(58.5, 157.5) * mm, "end": v(58.5, 217.5) * mm});
            skPoint(sketch, "E3.5.2.1", {"position": v(37.5, 187.5) * mm});
            skLineSegment(sketch, "E3.5.2.2", {"start": v(16.5, 157.5) * mm, "end": v(16.5, 217.5) * mm});
            skCircle(sketch, "E3.5.2.3", {"center": v(37.5, 187.5) * mm, "radius": 37.5 * mm, "construction": true});
            skLineSegment(sketch, "E3.5.2.4", {"start": v(58.5, 157.5) * mm, "end": v(16.5, 157.5) * mm});
            skLineSegment(sketch, "E3.5.2.5", {"start": v(58.5, 217.5) * mm, "end": v(16.5, 217.5) * mm});
            skLineSegment(sketch, "E3.5.3.0", {"start": v(58.5, 82.5) * mm, "end": v(58.5, 142.5) * mm});
            skPoint(sketch, "E3.5.3.1", {"position": v(37.5, 112.5) * mm});
            skLineSegment(sketch, "E3.5.3.2", {"start": v(16.5, 82.5) * mm, "end": v(16.5, 142.5) * mm});
            skCircle(sketch, "E3.5.3.3", {"center": v(37.5, 112.5) * mm, "radius": 37.5 * mm, "construction": true});
            skLineSegment(sketch, "E3.5.3.4", {"start": v(58.5, 82.5) * mm, "end": v(16.5, 82.5) * mm});
            skLineSegment(sketch, "E3.5.3.5", {"start": v(58.5, 142.5) * mm, "end": v(16.5, 142.5) * mm});
            skLineSegment(sketch, "E3.5.4.0", {"start": v(58.5, 7.5) * mm, "end": v(58.5, 67.5) * mm});
            skPoint(sketch, "E3.5.4.1", {"position": v(37.5, 37.5) * mm});
            skLineSegment(sketch, "E3.5.4.2", {"start": v(16.5, 7.5) * mm, "end": v(16.5, 67.5) * mm});
            skCircle(sketch, "E3.5.4.3", {"center": v(37.5, 37.5) * mm, "radius": 37.5 * mm, "construction": true});
            skLineSegment(sketch, "E3.5.4.4", {"start": v(58.5, 7.5) * mm, "end": v(16.5, 7.5) * mm});
            skLineSegment(sketch, "E3.5.4.5", {"start": v(58.5, 67.5) * mm, "end": v(16.5, 67.5) * mm});
            skLineSegment(sketch, "E3.5.5.0", {"start": v(58.5, -67.5) * mm, "end": v(58.5, -7.5) * mm});
            skPoint(sketch, "E3.5.5.1", {"position": v(37.5, -37.5) * mm});
            skLineSegment(sketch, "E3.5.5.2", {"start": v(16.5, -67.5) * mm, "end": v(16.5, -7.5) * mm});
            skCircle(sketch, "E3.5.5.3", {"center": v(37.5, -37.5) * mm, "radius": 37.5 * mm, "construction": true});
            skLineSegment(sketch, "E3.5.5.4", {"start": v(58.5, -67.5) * mm, "end": v(16.5, -67.5) * mm});
            skLineSegment(sketch, "E3.5.5.5", {"start": v(58.5, -7.5) * mm, "end": v(16.5, -7.5) * mm});
            skLineSegment(sketch, "E3.5.6.0", {"start": v(58.5, -142.5) * mm, "end": v(58.5, -82.5) * mm});
            skPoint(sketch, "E3.5.6.1", {"position": v(37.5, -112.5) * mm});
            skLineSegment(sketch, "E3.5.6.2", {"start": v(16.5, -142.5) * mm, "end": v(16.5, -82.5) * mm});
            skCircle(sketch, "E3.5.6.3", {"center": v(37.5, -112.5) * mm, "radius": 37.5 * mm, "construction": true});
            skLineSegment(sketch, "E3.5.6.4", {"start": v(58.5, -142.5) * mm, "end": v(16.5, -142.5) * mm});
            skLineSegment(sketch, "E3.5.6.5", {"start": v(58.5, -82.5) * mm, "end": v(16.5, -82.5) * mm});
            skLineSegment(sketch, "E3.5.7.0", {"start": v(58.5, -217.5) * mm, "end": v(58.5, -157.5) * mm});
            skPoint(sketch, "E3.5.7.1", {"position": v(37.5, -187.5) * mm});
            skLineSegment(sketch, "E3.5.7.2", {"start": v(16.5, -217.5) * mm, "end": v(16.5, -157.5) * mm});
            skCircle(sketch, "E3.5.7.3", {"center": v(37.5, -187.5) * mm, "radius": 37.5 * mm, "construction": true});
            skLineSegment(sketch, "E3.5.7.4", {"start": v(58.5, -217.5) * mm, "end": v(16.5, -217.5) * mm});
            skLineSegment(sketch, "E3.5.7.5", {"start": v(58.5, -157.5) * mm, "end": v(16.5, -157.5) * mm});
            skLineSegment(sketch, "E3.5.8.0", {"start": v(58.5, -292.5) * mm, "end": v(58.5, -232.5) * mm});
            skPoint(sketch, "E3.5.8.1", {"position": v(37.5, -262.5) * mm});
            skLineSegment(sketch, "E3.5.8.2", {"start": v(16.5, -292.5) * mm, "end": v(16.5, -232.5) * mm});
            skCircle(sketch, "E3.5.8.3", {"center": v(37.5, -262.5) * mm, "radius": 37.5 * mm, "construction": true});
            skLineSegment(sketch, "E3.5.8.4", {"start": v(58.5, -292.5) * mm, "end": v(16.5, -292.5) * mm});
            skLineSegment(sketch, "E3.5.8.5", {"start": v(58.5, -232.5) * mm, "end": v(16.5, -232.5) * mm});
            skLineSegment(sketch, "E3.5.9.0", {"start": v(58.5, -367.5) * mm, "end": v(58.5, -307.5) * mm});
            skPoint(sketch, "E3.5.9.1", {"position": v(37.5, -337.5) * mm});
            skLineSegment(sketch, "E3.5.9.2", {"start": v(16.5, -367.5) * mm, "end": v(16.5, -307.5) * mm});
            skCircle(sketch, "E3.5.9.3", {"center": v(37.5, -337.5) * mm, "radius": 37.5 * mm, "construction": true});
            skLineSegment(sketch, "E3.5.9.4", {"start": v(58.5, -367.5) * mm, "end": v(16.5, -367.5) * mm});
            skLineSegment(sketch, "E3.5.9.5", {"start": v(58.5, -307.5) * mm, "end": v(16.5, -307.5) * mm});
            skLineSegment(sketch, "E3.6.0.0", {"start": v(133.5, 307.5) * mm, "end": v(133.5, 367.5) * mm});
            skPoint(sketch, "E3.6.0.1", {"position": v(112.5, 337.5) * mm});
            skLineSegment(sketch, "E3.6.0.2", {"start": v(91.5, 307.5) * mm, "end": v(91.5, 367.5) * mm});
            skCircle(sketch, "E3.6.0.3", {"center": v(112.5, 337.5) * mm, "radius": 37.5 * mm, "construction": true});
            skLineSegment(sketch, "E3.6.0.4", {"start": v(133.5, 307.5) * mm, "end": v(91.5, 307.5) * mm});
            skLineSegment(sketch, "E3.6.0.5", {"start": v(133.5, 367.5) * mm, "end": v(91.5, 367.5) * mm});
            skLineSegment(sketch, "E3.6.1.0", {"start": v(133.5, 232.5) * mm, "end": v(133.5, 292.5) * mm});
            skPoint(sketch, "E3.6.1.1", {"position": v(112.5, 262.5) * mm});
            skLineSegment(sketch, "E3.6.1.2", {"start": v(91.5, 232.5) * mm, "end": v(91.5, 292.5) * mm});
            skCircle(sketch, "E3.6.1.3", {"center": v(112.5, 262.5) * mm, "radius": 37.5 * mm, "construction": true});
            skLineSegment(sketch, "E3.6.1.4", {"start": v(133.5, 232.5) * mm, "end": v(91.5, 232.5) * mm});
            skLineSegment(sketch, "E3.6.1.5", {"start": v(133.5, 292.5) * mm, "end": v(91.5, 292.5) * mm});
            skLineSegment(sketch, "E3.6.2.0", {"start": v(133.5, 157.5) * mm, "end": v(133.5, 217.5) * mm});
            skPoint(sketch, "E3.6.2.1", {"position": v(112.5, 187.5) * mm});
            skLineSegment(sketch, "E3.6.2.2", {"start": v(91.5, 157.5) * mm, "end": v(91.5, 217.5) * mm});
            skCircle(sketch, "E3.6.2.3", {"center": v(112.5, 187.5) * mm, "radius": 37.5 * mm, "construction": true});
            skLineSegment(sketch, "E3.6.2.4", {"start": v(133.5, 157.5) * mm, "end": v(91.5, 157.5) * mm});
            skLineSegment(sketch, "E3.6.2.5", {"start": v(133.5, 217.5) * mm, "end": v(91.5, 217.5) * mm});
            skLineSegment(sketch, "E3.6.3.0", {"start": v(133.5, 82.5) * mm, "end": v(133.5, 142.5) * mm});
            skPoint(sketch, "E3.6.3.1", {"position": v(112.5, 112.5) * mm});
            skLineSegment(sketch, "E3.6.3.2", {"start": v(91.5, 82.5) * mm, "end": v(91.5, 142.5) * mm});
            skCircle(sketch, "E3.6.3.3", {"center": v(112.5, 112.5) * mm, "radius": 37.5 * mm, "construction": true});
            skLineSegment(sketch, "E3.6.3.4", {"start": v(133.5, 82.5) * mm, "end": v(91.5, 82.5) * mm});
            skLineSegment(sketch, "E3.6.3.5", {"start": v(133.5, 142.5) * mm, "end": v(91.5, 142.5) * mm});
            skLineSegment(sketch, "E3.6.4.0", {"start": v(133.5, 7.5) * mm, "end": v(133.5, 67.5) * mm});
            skPoint(sketch, "E3.6.4.1", {"position": v(112.5, 37.5) * mm});
            skLineSegment(sketch, "E3.6.4.2", {"start": v(91.5, 7.5) * mm, "end": v(91.5, 67.5) * mm});
            skCircle(sketch, "E3.6.4.3", {"center": v(112.5, 37.5) * mm, "radius": 37.5 * mm, "construction": true});
            skLineSegment(sketch, "E3.6.4.4", {"start": v(133.5, 7.5) * mm, "end": v(91.5, 7.5) * mm});
            skLineSegment(sketch, "E3.6.4.5", {"start": v(133.5, 67.5) * mm, "end": v(91.5, 67.5) * mm});
            skLineSegment(sketch, "E3.6.5.0", {"start": v(133.5, -67.5) * mm, "end": v(133.5, -7.5) * mm});
            skPoint(sketch, "E3.6.5.1", {"position": v(112.5, -37.5) * mm});
            skLineSegment(sketch, "E3.6.5.2", {"start": v(91.5, -67.5) * mm, "end": v(91.5, -7.5) * mm});
            skCircle(sketch, "E3.6.5.3", {"center": v(112.5, -37.5) * mm, "radius": 37.5 * mm, "construction": true});
            skLineSegment(sketch, "E3.6.5.4", {"start": v(133.5, -67.5) * mm, "end": v(91.5, -67.5) * mm});
            skLineSegment(sketch, "E3.6.5.5", {"start": v(133.5, -7.5) * mm, "end": v(91.5, -7.5) * mm});
            skLineSegment(sketch, "E3.6.6.0", {"start": v(133.5, -142.5) * mm, "end": v(133.5, -82.5) * mm});
            skPoint(sketch, "E3.6.6.1", {"position": v(112.5, -112.5) * mm});
            skLineSegment(sketch, "E3.6.6.2", {"start": v(91.5, -142.5) * mm, "end": v(91.5, -82.5) * mm});
            skCircle(sketch, "E3.6.6.3", {"center": v(112.5, -112.5) * mm, "radius": 37.5 * mm, "construction": true});
            skLineSegment(sketch, "E3.6.6.4", {"start": v(133.5, -142.5) * mm, "end": v(91.5, -142.5) * mm});
            skLineSegment(sketch, "E3.6.6.5", {"start": v(133.5, -82.5) * mm, "end": v(91.5, -82.5) * mm});
            skLineSegment(sketch, "E3.6.7.0", {"start": v(133.5, -217.5) * mm, "end": v(133.5, -157.5) * mm});
            skPoint(sketch, "E3.6.7.1", {"position": v(112.5, -187.5) * mm});
            skLineSegment(sketch, "E3.6.7.2", {"start": v(91.5, -217.5) * mm, "end": v(91.5, -157.5) * mm});
            skCircle(sketch, "E3.6.7.3", {"center": v(112.5, -187.5) * mm, "radius": 37.5 * mm, "construction": true});
            skLineSegment(sketch, "E3.6.7.4", {"start": v(133.5, -217.5) * mm, "end": v(91.5, -217.5) * mm});
            skLineSegment(sketch, "E3.6.7.5", {"start": v(133.5, -157.5) * mm, "end": v(91.5, -157.5) * mm});
            skLineSegment(sketch, "E3.6.8.0", {"start": v(133.5, -292.5) * mm, "end": v(133.5, -232.5) * mm});
            skPoint(sketch, "E3.6.8.1", {"position": v(112.5, -262.5) * mm});
            skLineSegment(sketch, "E3.6.8.2", {"start": v(91.5, -292.5) * mm, "end": v(91.5, -232.5) * mm});
            skCircle(sketch, "E3.6.8.3", {"center": v(112.5, -262.5) * mm, "radius": 37.5 * mm, "construction": true});
            skLineSegment(sketch, "E3.6.8.4", {"start": v(133.5, -292.5) * mm, "end": v(91.5, -292.5) * mm});
            skLineSegment(sketch, "E3.6.8.5", {"start": v(133.5, -232.5) * mm, "end": v(91.5, -232.5) * mm});
            skLineSegment(sketch, "E3.6.9.0", {"start": v(133.5, -367.5) * mm, "end": v(133.5, -307.5) * mm});
            skPoint(sketch, "E3.6.9.1", {"position": v(112.5, -337.5) * mm});
            skLineSegment(sketch, "E3.6.9.2", {"start": v(91.5, -367.5) * mm, "end": v(91.5, -307.5) * mm});
            skCircle(sketch, "E3.6.9.3", {"center": v(112.5, -337.5) * mm, "radius": 37.5 * mm, "construction": true});
            skLineSegment(sketch, "E3.6.9.4", {"start": v(133.5, -367.5) * mm, "end": v(91.5, -367.5) * mm});
            skLineSegment(sketch, "E3.6.9.5", {"start": v(133.5, -307.5) * mm, "end": v(91.5, -307.5) * mm});
            skLineSegment(sketch, "E3.7.0.0", {"start": v(208.5, 307.5) * mm, "end": v(208.5, 367.5) * mm});
            skPoint(sketch, "E3.7.0.1", {"position": v(187.5, 337.5) * mm});
            skLineSegment(sketch, "E3.7.0.2", {"start": v(166.5, 307.5) * mm, "end": v(166.5, 367.5) * mm});
            skCircle(sketch, "E3.7.0.3", {"center": v(187.5, 337.5) * mm, "radius": 37.5 * mm, "construction": true});
            skLineSegment(sketch, "E3.7.0.4", {"start": v(208.5, 307.5) * mm, "end": v(166.5, 307.5) * mm});
            skLineSegment(sketch, "E3.7.0.5", {"start": v(208.5, 367.5) * mm, "end": v(166.5, 367.5) * mm});
            skLineSegment(sketch, "E3.7.1.0", {"start": v(208.5, 232.5) * mm, "end": v(208.5, 292.5) * mm});
            skPoint(sketch, "E3.7.1.1", {"position": v(187.5, 262.5) * mm});
            skLineSegment(sketch, "E3.7.1.2", {"start": v(166.5, 232.5) * mm, "end": v(166.5, 292.5) * mm});
            skCircle(sketch, "E3.7.1.3", {"center": v(187.5, 262.5) * mm, "radius": 37.5 * mm, "construction": true});
            skLineSegment(sketch, "E3.7.1.4", {"start": v(208.5, 232.5) * mm, "end": v(166.5, 232.5) * mm});
            skLineSegment(sketch, "E3.7.1.5", {"start": v(208.5, 292.5) * mm, "end": v(166.5, 292.5) * mm});
            skLineSegment(sketch, "E3.7.2.0", {"start": v(208.5, 157.5) * mm, "end": v(208.5, 217.5) * mm});
            skPoint(sketch, "E3.7.2.1", {"position": v(187.5, 187.5) * mm});
            skLineSegment(sketch, "E3.7.2.2", {"start": v(166.5, 157.5) * mm, "end": v(166.5, 217.5) * mm});
            skCircle(sketch, "E3.7.2.3", {"center": v(187.5, 187.5) * mm, "radius": 37.5 * mm, "construction": true});
            skLineSegment(sketch, "E3.7.2.4", {"start": v(208.5, 157.5) * mm, "end": v(166.5, 157.5) * mm});
            skLineSegment(sketch, "E3.7.2.5", {"start": v(208.5, 217.5) * mm, "end": v(166.5, 217.5) * mm});
            skLineSegment(sketch, "E3.7.3.0", {"start": v(208.5, 82.5) * mm, "end": v(208.5, 142.5) * mm});
            skPoint(sketch, "E3.7.3.1", {"position": v(187.5, 112.5) * mm});
            skLineSegment(sketch, "E3.7.3.2", {"start": v(166.5, 82.5) * mm, "end": v(166.5, 142.5) * mm});
            skCircle(sketch, "E3.7.3.3", {"center": v(187.5, 112.5) * mm, "radius": 37.5 * mm, "construction": true});
            skLineSegment(sketch, "E3.7.3.4", {"start": v(208.5, 82.5) * mm, "end": v(166.5, 82.5) * mm});
            skLineSegment(sketch, "E3.7.3.5", {"start": v(208.5, 142.5) * mm, "end": v(166.5, 142.5) * mm});
            skLineSegment(sketch, "E3.7.4.0", {"start": v(208.5, 7.5) * mm, "end": v(208.5, 67.5) * mm});
            skPoint(sketch, "E3.7.4.1", {"position": v(187.5, 37.5) * mm});
            skLineSegment(sketch, "E3.7.4.2", {"start": v(166.5, 7.5) * mm, "end": v(166.5, 67.5) * mm});
            skCircle(sketch, "E3.7.4.3", {"center": v(187.5, 37.5) * mm, "radius": 37.5 * mm, "construction": true});
            skLineSegment(sketch, "E3.7.4.4", {"start": v(208.5, 7.5) * mm, "end": v(166.5, 7.5) * mm});
            skLineSegment(sketch, "E3.7.4.5", {"start": v(208.5, 67.5) * mm, "end": v(166.5, 67.5) * mm});
            skLineSegment(sketch, "E3.7.5.0", {"start": v(208.5, -67.5) * mm, "end": v(208.5, -7.5) * mm});
            skPoint(sketch, "E3.7.5.1", {"position": v(187.5, -37.5) * mm});
            skLineSegment(sketch, "E3.7.5.2", {"start": v(166.5, -67.5) * mm, "end": v(166.5, -7.5) * mm});
            skCircle(sketch, "E3.7.5.3", {"center": v(187.5, -37.5) * mm, "radius": 37.5 * mm, "construction": true});
            skLineSegment(sketch, "E3.7.5.4", {"start": v(208.5, -67.5) * mm, "end": v(166.5, -67.5) * mm});
            skLineSegment(sketch, "E3.7.5.5", {"start": v(208.5, -7.5) * mm, "end": v(166.5, -7.5) * mm});
            skLineSegment(sketch, "E3.7.6.0", {"start": v(208.5, -142.5) * mm, "end": v(208.5, -82.5) * mm});
            skPoint(sketch, "E3.7.6.1", {"position": v(187.5, -112.5) * mm});
            skLineSegment(sketch, "E3.7.6.2", {"start": v(166.5, -142.5) * mm, "end": v(166.5, -82.5) * mm});
            skCircle(sketch, "E3.7.6.3", {"center": v(187.5, -112.5) * mm, "radius": 37.5 * mm, "construction": true});
            skLineSegment(sketch, "E3.7.6.4", {"start": v(208.5, -142.5) * mm, "end": v(166.5, -142.5) * mm});
            skLineSegment(sketch, "E3.7.6.5", {"start": v(208.5, -82.5) * mm, "end": v(166.5, -82.5) * mm});
            skLineSegment(sketch, "E3.7.7.0", {"start": v(208.5, -217.5) * mm, "end": v(208.5, -157.5) * mm});
            skPoint(sketch, "E3.7.7.1", {"position": v(187.5, -187.5) * mm});
            skLineSegment(sketch, "E3.7.7.2", {"start": v(166.5, -217.5) * mm, "end": v(166.5, -157.5) * mm});
            skCircle(sketch, "E3.7.7.3", {"center": v(187.5, -187.5) * mm, "radius": 37.5 * mm, "construction": true});
            skLineSegment(sketch, "E3.7.7.4", {"start": v(208.5, -217.5) * mm, "end": v(166.5, -217.5) * mm});
            skLineSegment(sketch, "E3.7.7.5", {"start": v(208.5, -157.5) * mm, "end": v(166.5, -157.5) * mm});
            skLineSegment(sketch, "E3.7.8.0", {"start": v(208.5, -292.5) * mm, "end": v(208.5, -232.5) * mm});
            skPoint(sketch, "E3.7.8.1", {"position": v(187.5, -262.5) * mm});
            skLineSegment(sketch, "E3.7.8.2", {"start": v(166.5, -292.5) * mm, "end": v(166.5, -232.5) * mm});
            skCircle(sketch, "E3.7.8.3", {"center": v(187.5, -262.5) * mm, "radius": 37.5 * mm, "construction": true});
            skLineSegment(sketch, "E3.7.8.4", {"start": v(208.5, -292.5) * mm, "end": v(166.5, -292.5) * mm});
            skLineSegment(sketch, "E3.7.8.5", {"start": v(208.5, -232.5) * mm, "end": v(166.5, -232.5) * mm});
            skLineSegment(sketch, "E3.7.9.0", {"start": v(208.5, -367.5) * mm, "end": v(208.5, -307.5) * mm});
            skPoint(sketch, "E3.7.9.1", {"position": v(187.5, -337.5) * mm});
            skLineSegment(sketch, "E3.7.9.2", {"start": v(166.5, -367.5) * mm, "end": v(166.5, -307.5) * mm});
            skCircle(sketch, "E3.7.9.3", {"center": v(187.5, -337.5) * mm, "radius": 37.5 * mm, "construction": true});
            skLineSegment(sketch, "E3.7.9.4", {"start": v(208.5, -367.5) * mm, "end": v(166.5, -367.5) * mm});
            skLineSegment(sketch, "E3.7.9.5", {"start": v(208.5, -307.5) * mm, "end": v(166.5, -307.5) * mm});
            skLineSegment(sketch, "E3.8.0.0", {"start": v(283.5, 307.5) * mm, "end": v(283.5, 367.5) * mm});
            skPoint(sketch, "E3.8.0.1", {"position": v(262.5, 337.5) * mm});
            skLineSegment(sketch, "E3.8.0.2", {"start": v(241.5, 307.5) * mm, "end": v(241.5, 367.5) * mm});
            skCircle(sketch, "E3.8.0.3", {"center": v(262.5, 337.5) * mm, "radius": 37.5 * mm, "construction": true});
            skLineSegment(sketch, "E3.8.0.4", {"start": v(283.5, 307.5) * mm, "end": v(241.5, 307.5) * mm});
            skLineSegment(sketch, "E3.8.0.5", {"start": v(283.5, 367.5) * mm, "end": v(241.5, 367.5) * mm});
            skLineSegment(sketch, "E3.8.1.0", {"start": v(283.5, 232.5) * mm, "end": v(283.5, 292.5) * mm});
            skPoint(sketch, "E3.8.1.1", {"position": v(262.5, 262.5) * mm});
            skLineSegment(sketch, "E3.8.1.2", {"start": v(241.5, 232.5) * mm, "end": v(241.5, 292.5) * mm});
            skCircle(sketch, "E3.8.1.3", {"center": v(262.5, 262.5) * mm, "radius": 37.5 * mm, "construction": true});
            skLineSegment(sketch, "E3.8.1.4", {"start": v(283.5, 232.5) * mm, "end": v(241.5, 232.5) * mm});
            skLineSegment(sketch, "E3.8.1.5", {"start": v(283.5, 292.5) * mm, "end": v(241.5, 292.5) * mm});
            skLineSegment(sketch, "E3.8.2.0", {"start": v(283.5, 157.5) * mm, "end": v(283.5, 217.5) * mm});
            skPoint(sketch, "E3.8.2.1", {"position": v(262.5, 187.5) * mm});
            skLineSegment(sketch, "E3.8.2.2", {"start": v(241.5, 157.5) * mm, "end": v(241.5, 217.5) * mm});
            skCircle(sketch, "E3.8.2.3", {"center": v(262.5, 187.5) * mm, "radius": 37.5 * mm, "construction": true});
            skLineSegment(sketch, "E3.8.2.4", {"start": v(283.5, 157.5) * mm, "end": v(241.5, 157.5) * mm});
            skLineSegment(sketch, "E3.8.2.5", {"start": v(283.5, 217.5) * mm, "end": v(241.5, 217.5) * mm});
            skLineSegment(sketch, "E3.8.3.0", {"start": v(283.5, 82.5) * mm, "end": v(283.5, 142.5) * mm});
            skPoint(sketch, "E3.8.3.1", {"position": v(262.5, 112.5) * mm});
            skLineSegment(sketch, "E3.8.3.2", {"start": v(241.5, 82.5) * mm, "end": v(241.5, 142.5) * mm});
            skCircle(sketch, "E3.8.3.3", {"center": v(262.5, 112.5) * mm, "radius": 37.5 * mm, "construction": true});
            skLineSegment(sketch, "E3.8.3.4", {"start": v(283.5, 82.5) * mm, "end": v(241.5, 82.5) * mm});
            skLineSegment(sketch, "E3.8.3.5", {"start": v(283.5, 142.5) * mm, "end": v(241.5, 142.5) * mm});
            skLineSegment(sketch, "E3.8.4.0", {"start": v(283.5, 7.5) * mm, "end": v(283.5, 67.5) * mm});
            skPoint(sketch, "E3.8.4.1", {"position": v(262.5, 37.5) * mm});
            skLineSegment(sketch, "E3.8.4.2", {"start": v(241.5, 7.5) * mm, "end": v(241.5, 67.5) * mm});
            skCircle(sketch, "E3.8.4.3", {"center": v(262.5, 37.5) * mm, "radius": 37.5 * mm, "construction": true});
            skLineSegment(sketch, "E3.8.4.4", {"start": v(283.5, 7.5) * mm, "end": v(241.5, 7.5) * mm});
            skLineSegment(sketch, "E3.8.4.5", {"start": v(283.5, 67.5) * mm, "end": v(241.5, 67.5) * mm});
            skLineSegment(sketch, "E3.8.5.0", {"start": v(283.5, -67.5) * mm, "end": v(283.5, -7.5) * mm});
            skPoint(sketch, "E3.8.5.1", {"position": v(262.5, -37.5) * mm});
            skLineSegment(sketch, "E3.8.5.2", {"start": v(241.5, -67.5) * mm, "end": v(241.5, -7.5) * mm});
            skCircle(sketch, "E3.8.5.3", {"center": v(262.5, -37.5) * mm, "radius": 37.5 * mm, "construction": true});
            skLineSegment(sketch, "E3.8.5.4", {"start": v(283.5, -67.5) * mm, "end": v(241.5, -67.5) * mm});
            skLineSegment(sketch, "E3.8.5.5", {"start": v(283.5, -7.5) * mm, "end": v(241.5, -7.5) * mm});
            skLineSegment(sketch, "E3.8.6.0", {"start": v(283.5, -142.5) * mm, "end": v(283.5, -82.5) * mm});
            skPoint(sketch, "E3.8.6.1", {"position": v(262.5, -112.5) * mm});
            skLineSegment(sketch, "E3.8.6.2", {"start": v(241.5, -142.5) * mm, "end": v(241.5, -82.5) * mm});
            skCircle(sketch, "E3.8.6.3", {"center": v(262.5, -112.5) * mm, "radius": 37.5 * mm, "construction": true});
            skLineSegment(sketch, "E3.8.6.4", {"start": v(283.5, -142.5) * mm, "end": v(241.5, -142.5) * mm});
            skLineSegment(sketch, "E3.8.6.5", {"start": v(283.5, -82.5) * mm, "end": v(241.5, -82.5) * mm});
            skLineSegment(sketch, "E3.8.7.0", {"start": v(283.5, -217.5) * mm, "end": v(283.5, -157.5) * mm});
            skPoint(sketch, "E3.8.7.1", {"position": v(262.5, -187.5) * mm});
            skLineSegment(sketch, "E3.8.7.2", {"start": v(241.5, -217.5) * mm, "end": v(241.5, -157.5) * mm});
            skCircle(sketch, "E3.8.7.3", {"center": v(262.5, -187.5) * mm, "radius": 37.5 * mm, "construction": true});
            skLineSegment(sketch, "E3.8.7.4", {"start": v(283.5, -217.5) * mm, "end": v(241.5, -217.5) * mm});
            skLineSegment(sketch, "E3.8.7.5", {"start": v(283.5, -157.5) * mm, "end": v(241.5, -157.5) * mm});
            skLineSegment(sketch, "E3.8.8.0", {"start": v(283.5, -292.5) * mm, "end": v(283.5, -232.5) * mm});
            skPoint(sketch, "E3.8.8.1", {"position": v(262.5, -262.5) * mm});
            skLineSegment(sketch, "E3.8.8.2", {"start": v(241.5, -292.5) * mm, "end": v(241.5, -232.5) * mm});
            skCircle(sketch, "E3.8.8.3", {"center": v(262.5, -262.5) * mm, "radius": 37.5 * mm, "construction": true});
            skLineSegment(sketch, "E3.8.8.4", {"start": v(283.5, -292.5) * mm, "end": v(241.5, -292.5) * mm});
            skLineSegment(sketch, "E3.8.8.5", {"start": v(283.5, -232.5) * mm, "end": v(241.5, -232.5) * mm});
            skLineSegment(sketch, "E3.8.9.0", {"start": v(283.5, -367.5) * mm, "end": v(283.5, -307.5) * mm});
            skPoint(sketch, "E3.8.9.1", {"position": v(262.5, -337.5) * mm});
            skLineSegment(sketch, "E3.8.9.2", {"start": v(241.5, -367.5) * mm, "end": v(241.5, -307.5) * mm});
            skCircle(sketch, "E3.8.9.3", {"center": v(262.5, -337.5) * mm, "radius": 37.5 * mm, "construction": true});
            skLineSegment(sketch, "E3.8.9.4", {"start": v(283.5, -367.5) * mm, "end": v(241.5, -367.5) * mm});
            skLineSegment(sketch, "E3.8.9.5", {"start": v(283.5, -307.5) * mm, "end": v(241.5, -307.5) * mm});
            skLineSegment(sketch, "E3.9.0.0", {"start": v(358.5, 307.5) * mm, "end": v(358.5, 367.5) * mm});
            skPoint(sketch, "E3.9.0.1", {"position": v(337.5, 337.5) * mm});
            skLineSegment(sketch, "E3.9.0.2", {"start": v(316.5, 307.5) * mm, "end": v(316.5, 367.5) * mm});
            skCircle(sketch, "E3.9.0.3", {"center": v(337.5, 337.5) * mm, "radius": 37.5 * mm, "construction": true});
            skLineSegment(sketch, "E3.9.0.4", {"start": v(358.5, 307.5) * mm, "end": v(316.5, 307.5) * mm});
            skLineSegment(sketch, "E3.9.0.5", {"start": v(358.5, 367.5) * mm, "end": v(316.5, 367.5) * mm});
            skLineSegment(sketch, "E3.9.1.0", {"start": v(358.5, 232.5) * mm, "end": v(358.5, 292.5) * mm});
            skPoint(sketch, "E3.9.1.1", {"position": v(337.5, 262.5) * mm});
            skLineSegment(sketch, "E3.9.1.2", {"start": v(316.5, 232.5) * mm, "end": v(316.5, 292.5) * mm});
            skCircle(sketch, "E3.9.1.3", {"center": v(337.5, 262.5) * mm, "radius": 37.5 * mm, "construction": true});
            skLineSegment(sketch, "E3.9.1.4", {"start": v(358.5, 232.5) * mm, "end": v(316.5, 232.5) * mm});
            skLineSegment(sketch, "E3.9.1.5", {"start": v(358.5, 292.5) * mm, "end": v(316.5, 292.5) * mm});
            skLineSegment(sketch, "E3.9.2.0", {"start": v(358.5, 157.5) * mm, "end": v(358.5, 217.5) * mm});
            skPoint(sketch, "E3.9.2.1", {"position": v(337.5, 187.5) * mm});
            skLineSegment(sketch, "E3.9.2.2", {"start": v(316.5, 157.5) * mm, "end": v(316.5, 217.5) * mm});
            skCircle(sketch, "E3.9.2.3", {"center": v(337.5, 187.5) * mm, "radius": 37.5 * mm, "construction": true});
            skLineSegment(sketch, "E3.9.2.4", {"start": v(358.5, 157.5) * mm, "end": v(316.5, 157.5) * mm});
            skLineSegment(sketch, "E3.9.2.5", {"start": v(358.5, 217.5) * mm, "end": v(316.5, 217.5) * mm});
            skLineSegment(sketch, "E3.9.3.0", {"start": v(358.5, 82.5) * mm, "end": v(358.5, 142.5) * mm});
            skPoint(sketch, "E3.9.3.1", {"position": v(337.5, 112.5) * mm});
            skLineSegment(sketch, "E3.9.3.2", {"start": v(316.5, 82.5) * mm, "end": v(316.5, 142.5) * mm});
            skCircle(sketch, "E3.9.3.3", {"center": v(337.5, 112.5) * mm, "radius": 37.5 * mm, "construction": true});
            skLineSegment(sketch, "E3.9.3.4", {"start": v(358.5, 82.5) * mm, "end": v(316.5, 82.5) * mm});
            skLineSegment(sketch, "E3.9.3.5", {"start": v(358.5, 142.5) * mm, "end": v(316.5, 142.5) * mm});
            skLineSegment(sketch, "E3.9.4.0", {"start": v(358.5, 7.5) * mm, "end": v(358.5, 67.5) * mm});
            skPoint(sketch, "E3.9.4.1", {"position": v(337.5, 37.5) * mm});
            skLineSegment(sketch, "E3.9.4.2", {"start": v(316.5, 7.5) * mm, "end": v(316.5, 67.5) * mm});
            skCircle(sketch, "E3.9.4.3", {"center": v(337.5, 37.5) * mm, "radius": 37.5 * mm, "construction": true});
            skLineSegment(sketch, "E3.9.4.4", {"start": v(358.5, 7.5) * mm, "end": v(316.5, 7.5) * mm});
            skLineSegment(sketch, "E3.9.4.5", {"start": v(358.5, 67.5) * mm, "end": v(316.5, 67.5) * mm});
            skLineSegment(sketch, "E3.9.5.0", {"start": v(358.5, -67.5) * mm, "end": v(358.5, -7.5) * mm});
            skPoint(sketch, "E3.9.5.1", {"position": v(337.5, -37.5) * mm});
            skLineSegment(sketch, "E3.9.5.2", {"start": v(316.5, -67.5) * mm, "end": v(316.5, -7.5) * mm});
            skCircle(sketch, "E3.9.5.3", {"center": v(337.5, -37.5) * mm, "radius": 37.5 * mm, "construction": true});
            skLineSegment(sketch, "E3.9.5.4", {"start": v(358.5, -67.5) * mm, "end": v(316.5, -67.5) * mm});
            skLineSegment(sketch, "E3.9.5.5", {"start": v(358.5, -7.5) * mm, "end": v(316.5, -7.5) * mm});
            skLineSegment(sketch, "E3.9.6.0", {"start": v(358.5, -142.5) * mm, "end": v(358.5, -82.5) * mm});
            skPoint(sketch, "E3.9.6.1", {"position": v(337.5, -112.5) * mm});
            skLineSegment(sketch, "E3.9.6.2", {"start": v(316.5, -142.5) * mm, "end": v(316.5, -82.5) * mm});
            skCircle(sketch, "E3.9.6.3", {"center": v(337.5, -112.5) * mm, "radius": 37.5 * mm, "construction": true});
            skLineSegment(sketch, "E3.9.6.4", {"start": v(358.5, -142.5) * mm, "end": v(316.5, -142.5) * mm});
            skLineSegment(sketch, "E3.9.6.5", {"start": v(358.5, -82.5) * mm, "end": v(316.5, -82.5) * mm});
            skLineSegment(sketch, "E3.9.7.0", {"start": v(358.5, -217.5) * mm, "end": v(358.5, -157.5) * mm});
            skPoint(sketch, "E3.9.7.1", {"position": v(337.5, -187.5) * mm});
            skLineSegment(sketch, "E3.9.7.2", {"start": v(316.5, -217.5) * mm, "end": v(316.5, -157.5) * mm});
            skCircle(sketch, "E3.9.7.3", {"center": v(337.5, -187.5) * mm, "radius": 37.5 * mm, "construction": true});
            skLineSegment(sketch, "E3.9.7.4", {"start": v(358.5, -217.5) * mm, "end": v(316.5, -217.5) * mm});
            skLineSegment(sketch, "E3.9.7.5", {"start": v(358.5, -157.5) * mm, "end": v(316.5, -157.5) * mm});
            skLineSegment(sketch, "E3.9.8.0", {"start": v(358.5, -292.5) * mm, "end": v(358.5, -232.5) * mm});
            skPoint(sketch, "E3.9.8.1", {"position": v(337.5, -262.5) * mm});
            skLineSegment(sketch, "E3.9.8.2", {"start": v(316.5, -292.5) * mm, "end": v(316.5, -232.5) * mm});
            skCircle(sketch, "E3.9.8.3", {"center": v(337.5, -262.5) * mm, "radius": 37.5 * mm, "construction": true});
            skLineSegment(sketch, "E3.9.8.4", {"start": v(358.5, -292.5) * mm, "end": v(316.5, -292.5) * mm});
            skLineSegment(sketch, "E3.9.8.5", {"start": v(358.5, -232.5) * mm, "end": v(316.5, -232.5) * mm});
            skLineSegment(sketch, "E3.9.9.0", {"start": v(358.5, -367.5) * mm, "end": v(358.5, -307.5) * mm});
            skPoint(sketch, "E3.9.9.1", {"position": v(337.5, -337.5) * mm});
            skLineSegment(sketch, "E3.9.9.2", {"start": v(316.5, -367.5) * mm, "end": v(316.5, -307.5) * mm});
            skCircle(sketch, "E3.9.9.3", {"center": v(337.5, -337.5) * mm, "radius": 37.5 * mm, "construction": true});
            skLineSegment(sketch, "E3.9.9.4", {"start": v(358.5, -367.5) * mm, "end": v(316.5, -367.5) * mm});
            skLineSegment(sketch, "E3.9.9.5", {"start": v(358.5, -307.5) * mm, "end": v(316.5, -307.5) * mm});
            skLineSegment(sketch, "E3.direction1", {"start": v(-358.5, 307.5) * mm, "end": v(-283.5, 307.5) * mm, "construction": true});
            skLineSegment(sketch, "E3.direction2", {"start": v(-358.5, 307.5) * mm, "end": v(-358.5, 232.5) * mm, "construction": true});
            skSolve(sketch);
        }
        {
            var Q0;
            Q0 = qSketchRegion(id + "F2", true);
            extrude(context, id + "F3", {"entities" : qUnion([Q0]), "operationType" : NewBodyOperationType.REMOVE, "oppositeDirection" : true, "depth" : 4 * mm});
        }
    });
